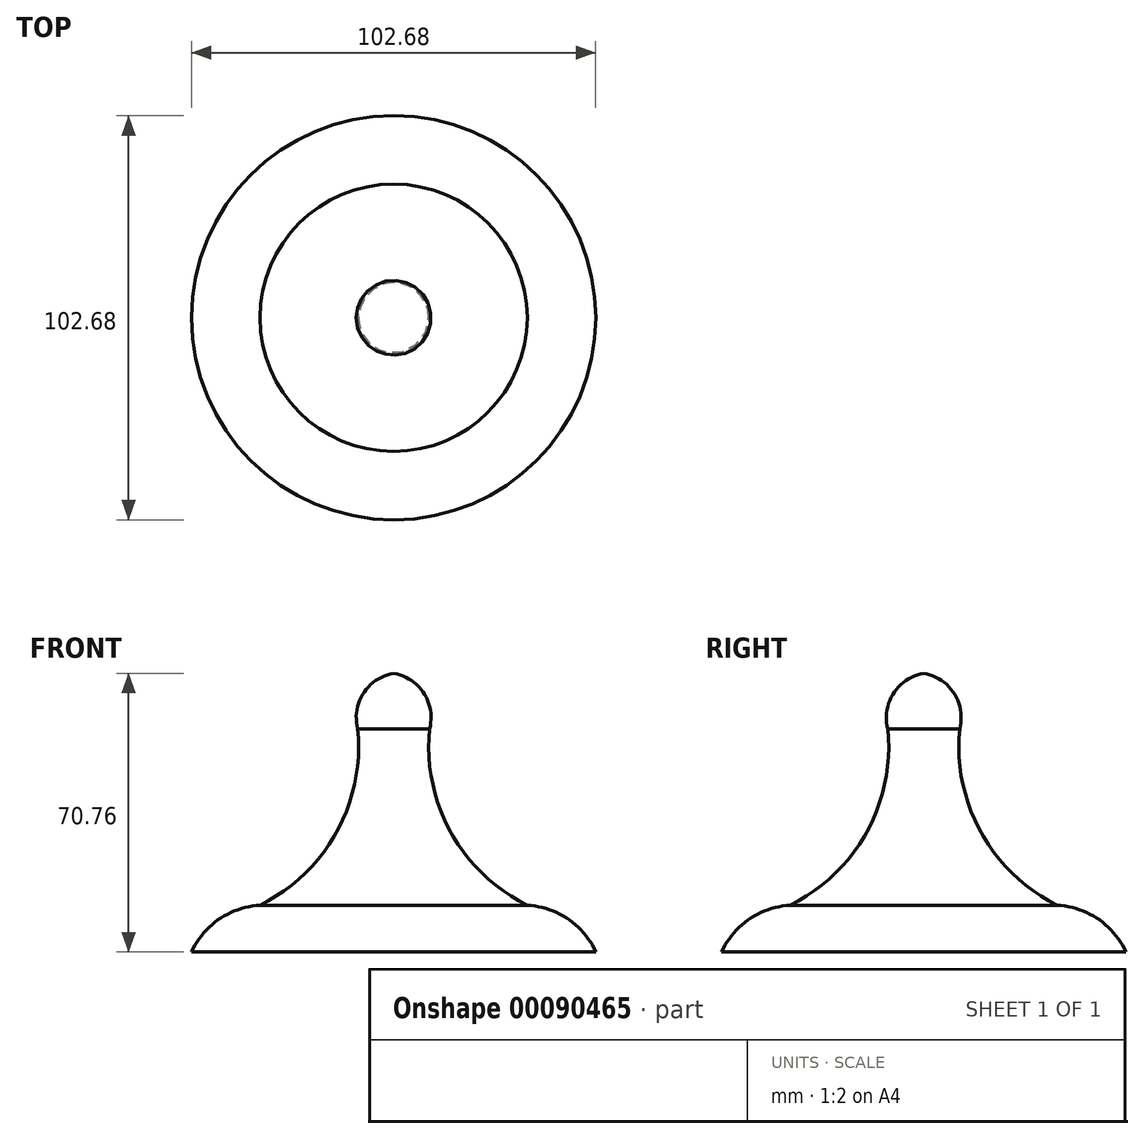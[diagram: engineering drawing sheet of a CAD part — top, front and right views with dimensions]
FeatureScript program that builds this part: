
annotation { "Feature Type Name" : "Feature", "Feature Type Description" : "" }
export const myFeature = defineFeature(function(context is Context, id is Id, definition is map)
    precondition{}
    {
        {
            var Q0;
            Q0=qCreatedBy(makeId("Front.planeOp"),FACE);
            var sketch = newSketch(context, id + "F0", { "sketchPlane" : qUnion([Q0])});
            skArc(sketch, "E0", {"start": v(51.34, 0) * mm, "mid": v(44.3, 8.34) * mm, "end": v(33.94, 11.84) * mm});
            skArc(sketch, "E1", {"start": v(9.13, 56.62) * mm, "mid": v(14.53, 30.35) * mm, "end": v(33.94, 11.84) * mm});
            skArc(sketch, "E2", {"start": v(9.13, 56.62) * mm, "mid": v(7.68, 65.7) * mm, "end": v(0, 70.76) * mm});
            skLineSegment(sketch, "E3", {"start": v(0, 70.76) * mm, "end": v(0, 0) * mm});
            skLineSegment(sketch, "E4", {"start": v(0, 0) * mm, "end": v(51.34, 0) * mm});
            skSolve(sketch);
        }
        {
            var Q0;
            Q0=makeQuery(id+"F0.imprint","IMPRINT",FACE,{"disambiguationData":[TD([[makeQuery(id+"F0.imprint","IMPRINT",EDGE,{"derivedFrom":sQuery(id+"F0.wireOp",EDGE,"E0")}),1.0]])]});
            var Q1;
            Q1=sQuery(id+"F0.wireOp",EDGE,"E3");
            revolve(context, id + "F1", {"entities" : qUnion([Q0]), "axis" : qUnion([Q1]), "revolveType" : RevolveType.FULL});
        }
    });
